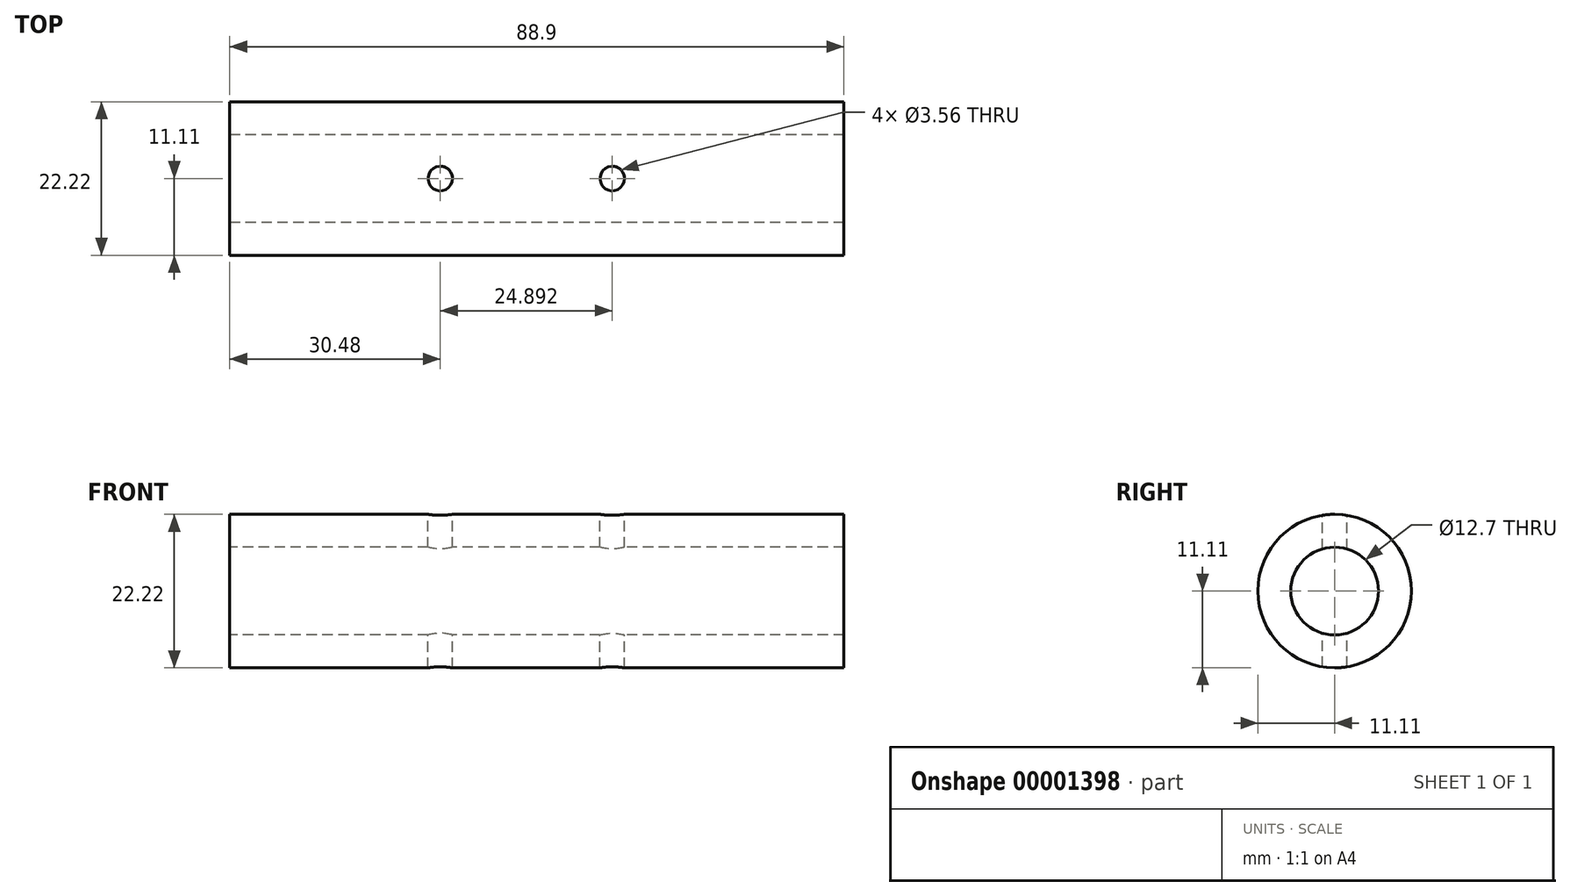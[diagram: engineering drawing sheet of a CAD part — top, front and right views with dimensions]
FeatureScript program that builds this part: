
annotation { "Feature Type Name" : "Feature", "Feature Type Description" : "" }
export const myFeature = defineFeature(function(context is Context, id is Id, definition is map)
    precondition{}
    {
        {
            var Q0;
            Q0=qCreatedBy(makeId("Right.planeOp"),FACE);
            var sketch = newSketch(context, id + "F0", { "sketchPlane" : qUnion([Q0])});
            skCircle(sketch, "E0", {"center": v(0, 0) * mm, "radius": 11.11 * mm});
            skCircle(sketch, "E1", {"center": v(0, 0) * mm, "radius": 6.35 * mm});
            skSolve(sketch);
        }
        {
            var Q0;
            Q0 = qSketchRegion(id + "F0", true);
            extrude(context, id + "F1", {"entities" : qUnion([Q0]), "endBound" : BoundingType.SYMMETRIC, "depth" : 88.9 * mm});
        }
        {
            var Q0;
            Q0=qCreatedBy(makeId("Top.planeOp"),FACE);
            var sketch = newSketch(context, id + "F2", { "sketchPlane" : qUnion([Q0])});
            skCircle(sketch, "E2", {"center": v(-13.97, 0) * mm, "radius": 1.78 * mm});
            skCircle(sketch, "E3", {"center": v(10.92, 0) * mm, "radius": 1.78 * mm});
            skSolve(sketch);
        }
        {
            var Q0;
            Q0 = qSketchRegion(id + "F2", true);
            extrude(context, id + "F3", {"entities" : qUnion([Q0]), "operationType" : NewBodyOperationType.REMOVE, "endBound" : BoundingType.SYMMETRIC, "oppositeDirection" : true, "depth" : 27.26 * mm});
        }
    });
